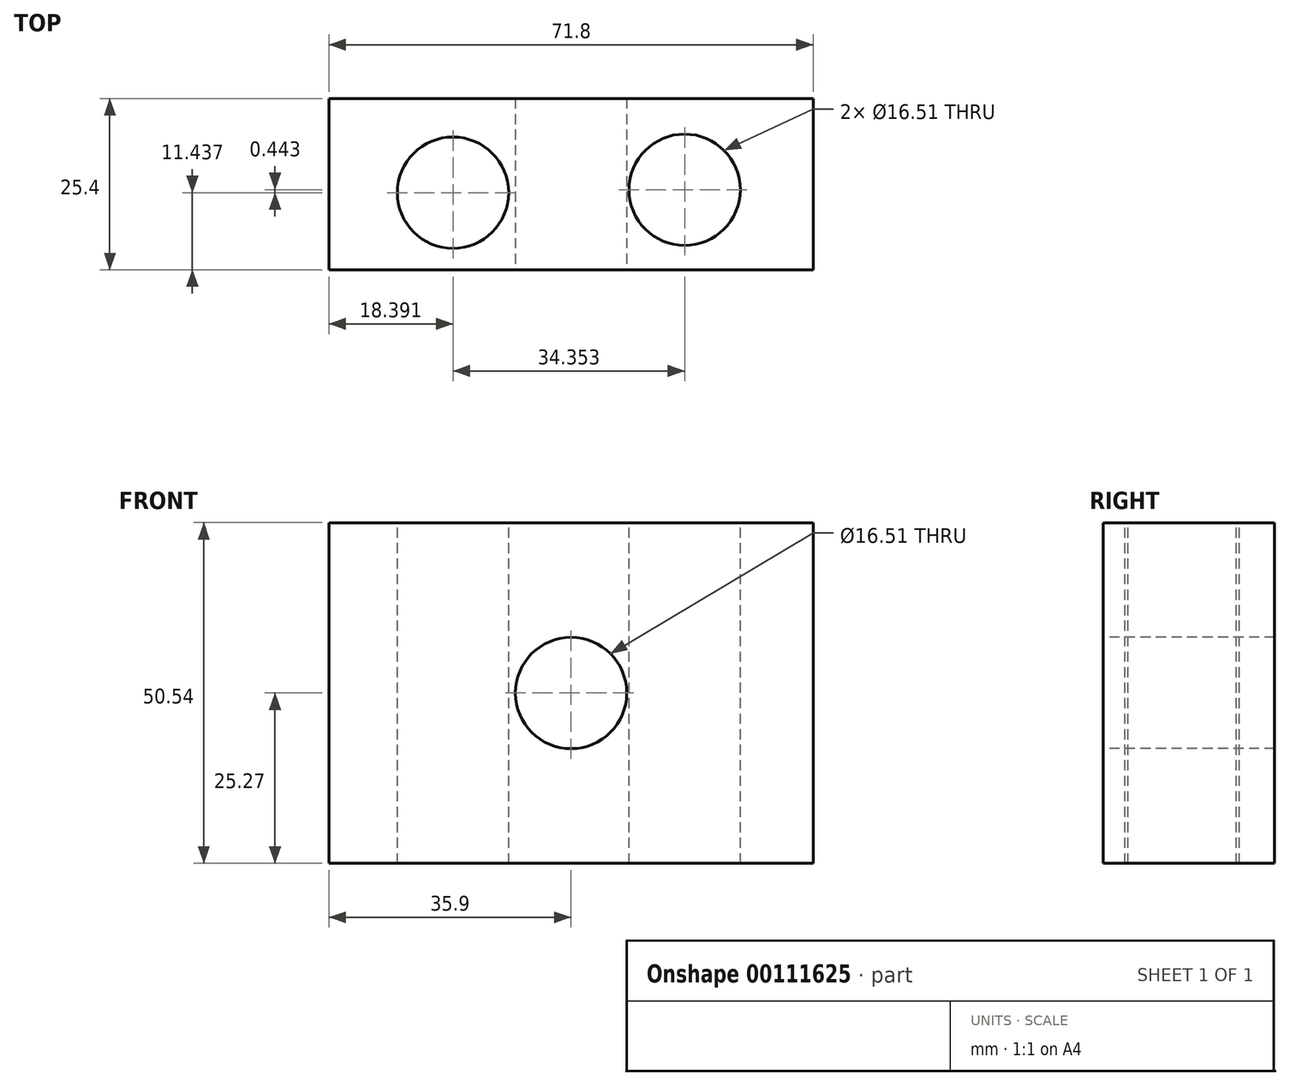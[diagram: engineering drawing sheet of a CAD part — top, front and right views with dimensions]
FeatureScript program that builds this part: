
annotation { "Feature Type Name" : "Feature", "Feature Type Description" : "" }
export const myFeature = defineFeature(function(context is Context, id is Id, definition is map)
    precondition{}
    {
        {
            var Q0;
            Q0=qCreatedBy(makeId("Front.planeOp"),FACE);
            var sketch = newSketch(context, id + "F0", { "sketchPlane" : qUnion([Q0])});
            skLineSegment(sketch, "E0.bottom", {"start": v(-35.9, -25.27) * mm, "end": v(35.9, -25.27) * mm});
            skLineSegment(sketch, "E0.top", {"start": v(-35.9, 25.27) * mm, "end": v(35.9, 25.27) * mm});
            skLineSegment(sketch, "E0.left", {"start": v(-35.9, -25.27) * mm, "end": v(-35.9, 25.27) * mm});
            skLineSegment(sketch, "E0.right", {"start": v(35.9, -25.27) * mm, "end": v(35.9, 25.27) * mm});
            skPoint(sketch, "E0.middle", {"position": v(0, 0) * mm});
            skSolve(sketch);
        }
        {
            var Q0;
            Q0=makeQuery(id+"F0.imprint","IMPRINT",FACE,{"disambiguationData":[TD([[makeQuery(id+"F0.imprint","IMPRINT",EDGE,{"derivedFrom":sQuery(id+"F0.wireOp",EDGE,"E0.bottom")}),1.0]])]});
            extrude(context, id + "F1", {"entities" : qUnion([Q0]), "depth" : 25.4 * mm});
        }
        {
            var Q0;
            Q0=makeQuery(id+"F1.opExtrude","CAP_FACE",FACE,{"disambiguationData":[OSD([sQuery(id+"F0.wireOp",EDGE,"E0.bottom"),sQuery(id+"F0.wireOp",EDGE,"E0.top"),sQuery(id+"F0.wireOp",EDGE,"E0.left"),sQuery(id+"F0.wireOp",EDGE,"E0.right")])],"isStart":false});
            var sketch = newSketch(context, id + "F2", { "sketchPlane" : qUnion([Q0])});
            skCircle(sketch, "E1", {"center": v(0, 0) * mm, "radius": 7.22 * mm});
            skSolve(sketch);
        }
        {
            var Q0;
            Q0=sQuery(id+"F2.wireOp",VERTEX,"E1.center");
            var Q1;
            Q1=makeQuery(id+"F1.opExtrude","SWEPT_BODY",BODY,{"disambiguationData":[OSD([sQuery(id+"F0.wireOp",EDGE,"E0.bottom"),sQuery(id+"F0.wireOp",EDGE,"E0.top"),sQuery(id+"F0.wireOp",EDGE,"E0.left"),sQuery(id+"F0.wireOp",EDGE,"E0.right")])]});
            hole(context, id + "F3", {"style" : HoleStyle.SIMPLE, "endStyle" : HoleEndStyle.THROUGH, "holeDiameter" : 16.5 * mm, "locations" : qUnion([Q0]), "scope" : qUnion([Q1]), "isTappedThrough" : true});
        }
        {
            var Q0;
            Q0=makeQuery(id+"F1.opExtrude","SWEPT_FACE",FACE,{"disambiguationData":[OSD([sQuery(id+"F0.wireOp",EDGE,"E0.top")])]});
            var sketch = newSketch(context, id + "F4", { "sketchPlane" : qUnion([Q0])});
            skCircle(sketch, "E2", {"center": v(16.84, -13.52) * mm, "radius": 5.6 * mm});
            skCircle(sketch, "E3", {"center": v(-17.5, -13.96) * mm, "radius": 5.89 * mm});
            skSolve(sketch);
        }
        {
            var Q0;
            Q0=sQuery(id+"F4.wireOp",VERTEX,"E3.center");
            var Q1;
            Q1=sQuery(id+"F4.wireOp",VERTEX,"E2.center");
            var Q2;
            Q2=makeQuery(id+"F1.opExtrude","SWEPT_BODY",BODY,{"disambiguationData":[OSD([sQuery(id+"F0.wireOp",EDGE,"E0.bottom"),sQuery(id+"F0.wireOp",EDGE,"E0.top"),sQuery(id+"F0.wireOp",EDGE,"E0.left"),sQuery(id+"F0.wireOp",EDGE,"E0.right")])]});
            hole(context, id + "F5", {"style" : HoleStyle.SIMPLE, "endStyle" : HoleEndStyle.THROUGH, "holeDiameter" : 16.5 * mm, "locations" : qUnion([Q0, Q1]), "scope" : qUnion([Q2]), "isTappedThrough" : true});
        }
    });
